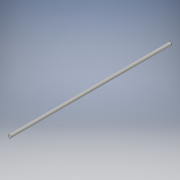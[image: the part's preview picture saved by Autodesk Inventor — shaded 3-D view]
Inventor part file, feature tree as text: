
AUTODESK INVENTOR PART (.ipt)
format: ipt  version: 2016 (Build 200138000, 138)  size: 86,016 bytes
history: native  units: in
note: dims shown in document units (in); Inventor stores cm internally (conversion verified against a paired STEP export)
features: extrude x1, sketch x1
ambient origin geometry x8: Origin, YZ Plane, XZ Plane, XY Plane, X Axis, Y Axis, Z Axis, Center Point
bodies: Solid1 (feature_tree)
feature tree (2):
  extrude  "Extrusion1"  Depth=10.0in TaperAngle=0.0deg
  sketch  "Sketch1"  dims[d0=0.188in d1=10.0in d2=0.0in]
